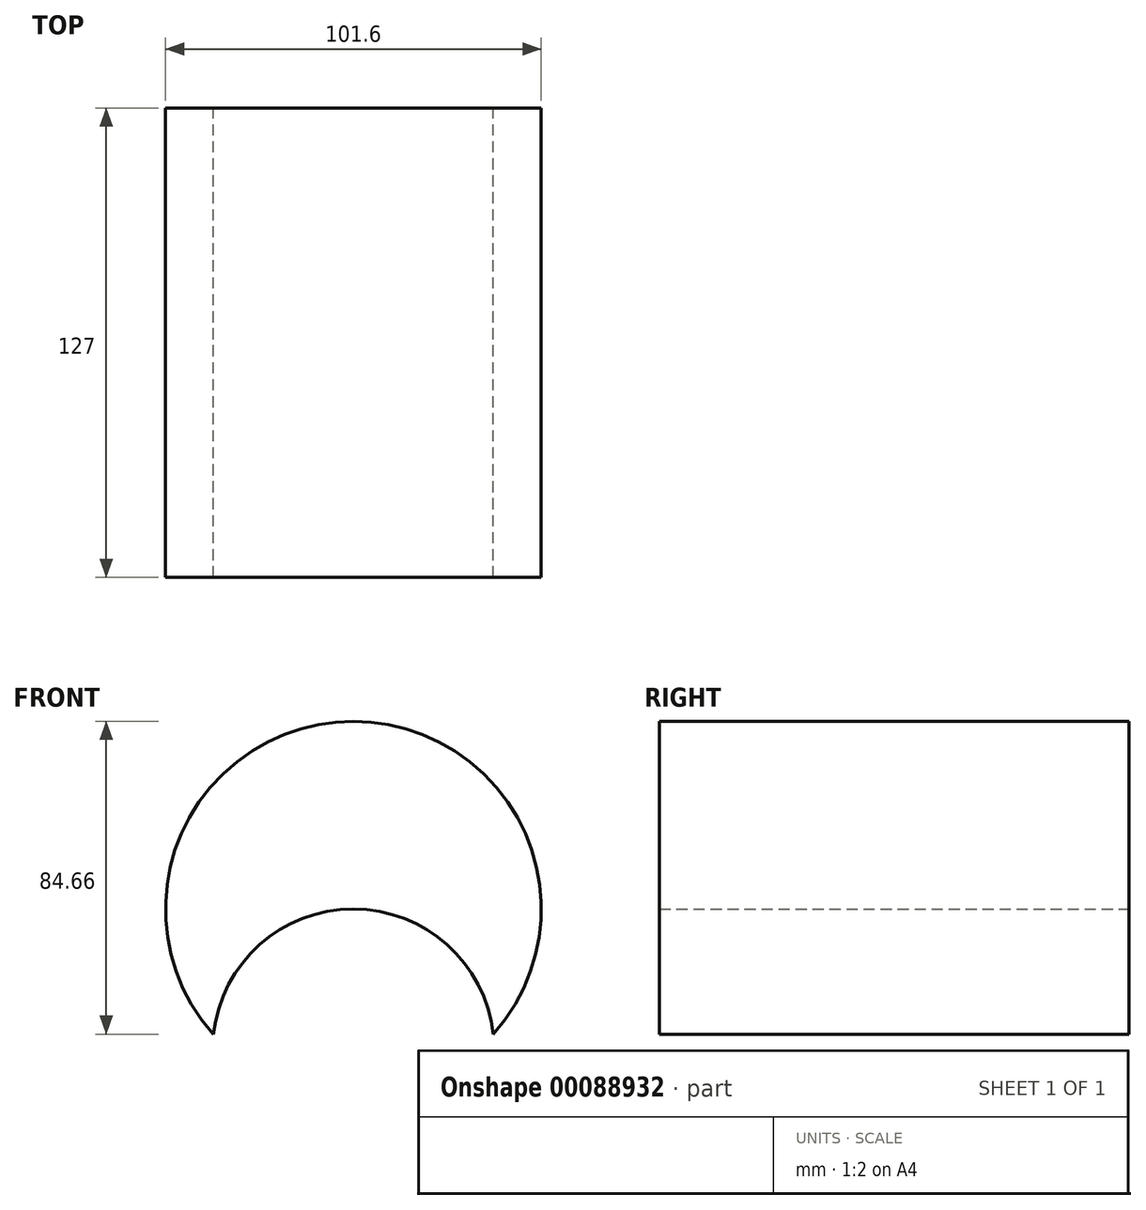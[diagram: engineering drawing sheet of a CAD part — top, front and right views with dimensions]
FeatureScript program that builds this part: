
annotation { "Feature Type Name" : "Feature", "Feature Type Description" : "" }
export const myFeature = defineFeature(function(context is Context, id is Id, definition is map)
    precondition{}
    {
        {
            var Q0;
            Q0=qCreatedBy(makeId("Front.planeOp"),FACE);
            var sketch = newSketch(context, id + "F0", { "sketchPlane" : qUnion([Q0])});
            skCircle(sketch, "E0", {"center": v(0, -14.14) * mm, "radius": 50.8 * mm});
            skCircle(sketch, "E1", {"center": v(0, -52.24) * mm, "radius": 38.1 * mm});
            skSolve(sketch);
        }
        {
            var Q0;
            {var subQ0=sQuery(id+"F0.wireOp",EDGE,"E1");var subQ1=sQuery(id+"F0.wireOp",EDGE,"E0");var subQ2=makeQuery(id+"F0.imprint","INTERSECT",VERTEX,{"disambiguationData":[OD(0.0)],"derivedFrom":[subQ1,subQ0]});Q0=makeQuery(id+"F0.imprint","IMPRINT",FACE,{"disambiguationData":[TD([[makeQuery(id+"F0.imprint","IMPRINT",EDGE,{"disambiguationData":[TD([[subQ2,-1.0]])],"derivedFrom":subQ1}),-1.0]])]});}
            var sketch = newSketch(context, id + "F1", { "sketchPlane" : qUnion([Q0])});
            skSolve(sketch);
        }
        {
            var Q0;
            {var subQ0=sQuery(id+"F0.wireOp",EDGE,"E1");var subQ1=sQuery(id+"F0.wireOp",EDGE,"E0");var subQ2=makeQuery(id+"F0.imprint","INTERSECT",VERTEX,{"disambiguationData":[OD(0.0)],"derivedFrom":[subQ1,subQ0]});Q0=makeQuery(id+"F1.imprint","IMPRINT",FACE,{"disambiguationData":[TD([[makeQuery(id+"F1.imprint","IMPRINT",EDGE,{"derivedFrom":makeQuery(id+"F0.imprint","IMPRINT",EDGE,{"disambiguationData":[TD([[subQ2,-1.0]])],"derivedFrom":subQ1})}),-1.0]])]});}
            var sketch = newSketch(context, id + "F2", { "sketchPlane" : qUnion([Q0])});
            skSolve(sketch);
        }
        {
            var Q0;
            {var subQ0=sQuery(id+"F0.wireOp",EDGE,"E1");var subQ1=sQuery(id+"F0.wireOp",EDGE,"E0");var subQ2=makeQuery(id+"F0.imprint","INTERSECT",VERTEX,{"disambiguationData":[OD(0.0)],"derivedFrom":[subQ1,subQ0]});Q0=makeQuery(id+"F0.imprint","IMPRINT",FACE,{"disambiguationData":[TD([[makeQuery(id+"F0.imprint","IMPRINT",EDGE,{"disambiguationData":[TD([[subQ2,1.0]])],"derivedFrom":subQ1}),1.0]])]});}
            extrude(context, id + "F3", {"entities" : qUnion([Q0]), "depth" : 127 * mm});
        }
        {
            var Q0;
            Q0=qCreatedBy(makeId("Top.planeOp"),FACE);
            var sketch = newSketch(context, id + "F4", { "sketchPlane" : qUnion([Q0])});
            skCircle(sketch, "E2", {"center": v(0, -71.22) * mm, "radius": 21 * mm});
            skSolve(sketch);
        }
        {
            var Q0;
            Q0=sQuery(id+"F4.wireOp",EDGE,"E2");
            extrude(context, id + "F5", {"bodyType" : ToolBodyType.SURFACE, "surfaceEntities" : qUnion([Q0]), "endBound" : BoundingType.THROUGH_ALL, "depth" : 25.4 * mm});
        }
    });
